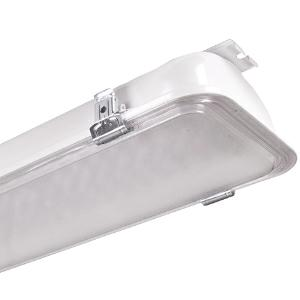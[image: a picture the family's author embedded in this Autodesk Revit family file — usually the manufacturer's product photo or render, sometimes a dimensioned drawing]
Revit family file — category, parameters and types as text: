
# Revit family: 3f_filippi_-_beta_235_75_pc_medio_3f_filippi_-_52560_-_beta_235_led_751x60_dali_medio_l1565
name_source: partatom
category: Lighting Fixtures
units: mm (PartAtom-declared; Revit-internal decimal feet)

## family parameters
Cut with Voids When Loaded = No
Host = Face
Light Source = No
Part Type = Normal
Room Calculation Point = No
Round Connector Dimension = Use Diameter
Shared = No

## types (1)
- 3F Filippi - Beta 235 75 PC Medio (1 x LED, 9781 lm, 65 W, 4000 K)
    Apparent Load = 65 VA
    Approval mark = CE
    CIE Flux Codes = 68 91 99 100 100
    Color Rendering = 80
    Color Temperature = 4000 K
    Control Gear = Electronic transformer
    Default Elevation = 1800 mm
    Description = ILLUMINOTECHNICAL
Luminous efficiency 100% (DLOR 99%, ULOR 1%).
Initial luminous flux of the luminaire 9781 lm.
Medium symmetric distribution.
Installation Interdistance Transv.D = 1.16 x hu - Long.D = 1.16 x hu.
Average luminance <3000 cd/m² for radial angles >65°.
Tabular UGR (CIE 117 - 4H-8H; S=0.25H; 70/50/20): RUG 18.4 - 18.8.
Beam angle: 76° - 76°.
Luminous efficacy 150 lm/W.
Lifetime (L93/B10): 30000 h. (tq+25°C)
Lifetime (L90/B10): 50000 h. (tq+25°C)
Lifetime (L85/B10): 80000 h. (tq+25°C)
Lifetime (L80/B10): 100000 h. (tq+25°C)
Lifetime (L85/B10): 50000 h. (tq+45°C)
Sudden decreased luminous flux after 50000 hours: 0% (C0).
Photobiological safety in compliance with IEC/TR 62778: RG0 risk exempt, (IEC 62471).
In compliance with IEC/EN 62722-2-1 - IEC/EN 62717 standards.

SOURCE
Linear LED module 60W/840.
Energy efficiency class (UE 2019/2020 - UE 2019/2015): C.
CIE 13.3 Colour rendering index: CRI >80 (R9 <50%).
IES TM-30 Fidelity Index: Rf = 84 Rg = 95.
CCT nominal colour temperature 4000 K.
Colour initial tolerance (MacAdam): SDCM 3.

MECHANICAL
Single-piece housing in pressed steel, powder-coated in white epoxy-polyester.
Polycarbonate screen etched internally, V2 self-extinguishing, UV stabilised, injection moulded.
Ecologic anti-aging injected sealing gasket.
Oversized gear-tray reflector unit in highly reflective white painted hot-galvanised steel.
Methacrylate (PMMA) lenses with external flat surface.
Galvanised steel snap-lock clips for diffuser mounting (safety n° 4 per fixture).
Luminaire with limited surface temperature. - D - (EN 60598-2-24)
Dimensions: 1565x235 mm, height 107 mm. Weight 7.75 kg.
IP65 protection degree.
Mechanical strength to impacts IK09 (10 joule).
Glow-wire test resistance 850°C.

ELECTRICAL
Halogen Free DALI-2, PUSH-DIM, electronic wiring 230V-50/60Hz, power factor 0.95 at full load, THD <25%, constant output current, class I, 1 driver, 1 DALI addresse.
Power of the luminaire 65 W.
ENEC - CE.
Flicker: <4%.
Luminaire compliant with EN 60598-2-22 for power supply from a centralised emergency system CPSS (Central Power Supply System), not incorporated in the luminaire - high risk areas excluded. The default power and flux are 100% in AC and 15% in DC.
Ambient temperature from -20°C to +45°C.
Temperature class T6 max 85°C.
Quick connection via M25 5P connector with 9-13 mm tightening range.
Relative humidity UR: <85%.

INSTALLATION
Ceiling / Suspended / Wall.
All accessories dedicated to this product are available on the Catalog and on our website www.3F-Filippi.com.

APPLICATIONS
Suitable product for food production plants (HACCP), IFS (Food Version 6), BRC (GSFS Food Version 7).
Dry, dusty indoor environments, subject to occasional water splashes.
Industrial environments, warehouses, environments where security locks are required on all clips, e.g. prisons (on request).
Environments in which it is necessary a total protection against falling fragments (eg environments with foodstuffs or machines with moving parts or with extreme temperature changes), use luminaires with laminated glass.
Tempered glass is not immune to falling fragments from harmless and caused by shocks or exceptionally derived from the tempering process.

LIGHT MANAGEMENT
Recommended minimum setting: 10%.
The device, equipped with DALI-2 driver, can be controlled manually with 3F Easy Dim technology or automatically/manually with 3F Smart Dimming technology and/or centralised DALI systems.
DALI-2 certification guarantees interoperability with other devices with the same certification.
In electrical systems without a regulation system (manual or automatic) and DALI bus, a suitable jumper must be made on the DA-DA terminals of the appliance.

WARNING
Fixture not suitable for cold stores with an ambient temperature <0°C and/or relative humidity >85%.
Luminaire designed for disposal/recycling at end-of-life.
Replaceable (LED only) light source by a professional. Replaceable control gear by a professional.
    Height = 107 mm
    Lamp = 1 x LED
    Lamp Light Flux = 9781 lm
    Lamp Power = 65 W
    Lamp count = 1
    Length = 1565 mm
    Lifetime = 50000 h
    Luminous efficacy = 150 lm/W
    Manufacturer = 3F Filippi
    ModVariant = No
    Model = 3F Filippi - 52560 - Beta 235 LED 751x60 DALI MEDIO L1565
    Mounting Place = Ceiling
    Mounting Type = Pendant
    Number of Poles = 1
    OnlyDefault = Yes
    Power Factor = 1
    Product Name = 3F Filippi - Beta 235 75 PC Medio
    Product group = pendant luminaire
    ProductGroupID = 9
    Protection Class = Protection class I
    Protection Degree = IP 65
    RLX_Detail_Level = 1
    RLX_Emergency_Light_Flux = 0 lm
    RLX_Emergency_Type = 0
    RLX_Emergency_Type_DB = No
    RlxData = <blob elided: 85361 chars, md5=07267625>
    Socket = socket
    Standby Power = 0 W
    System Light Flux = 9781 lm
    System Power = 65 W
    Type Comments = Product without accessories
    Type Image = 3ffilippi_beta_235_led_75_l1565.jpg
    URL = http://relux.com
    VarID = ---
    Voltage = 0 V
    Weight = 0.00 kg
    Width = 235 mm

## geometry (parser evidence)
native form markers: Blend x4, Sweep x13
no freeform markers — native parametric forms only
